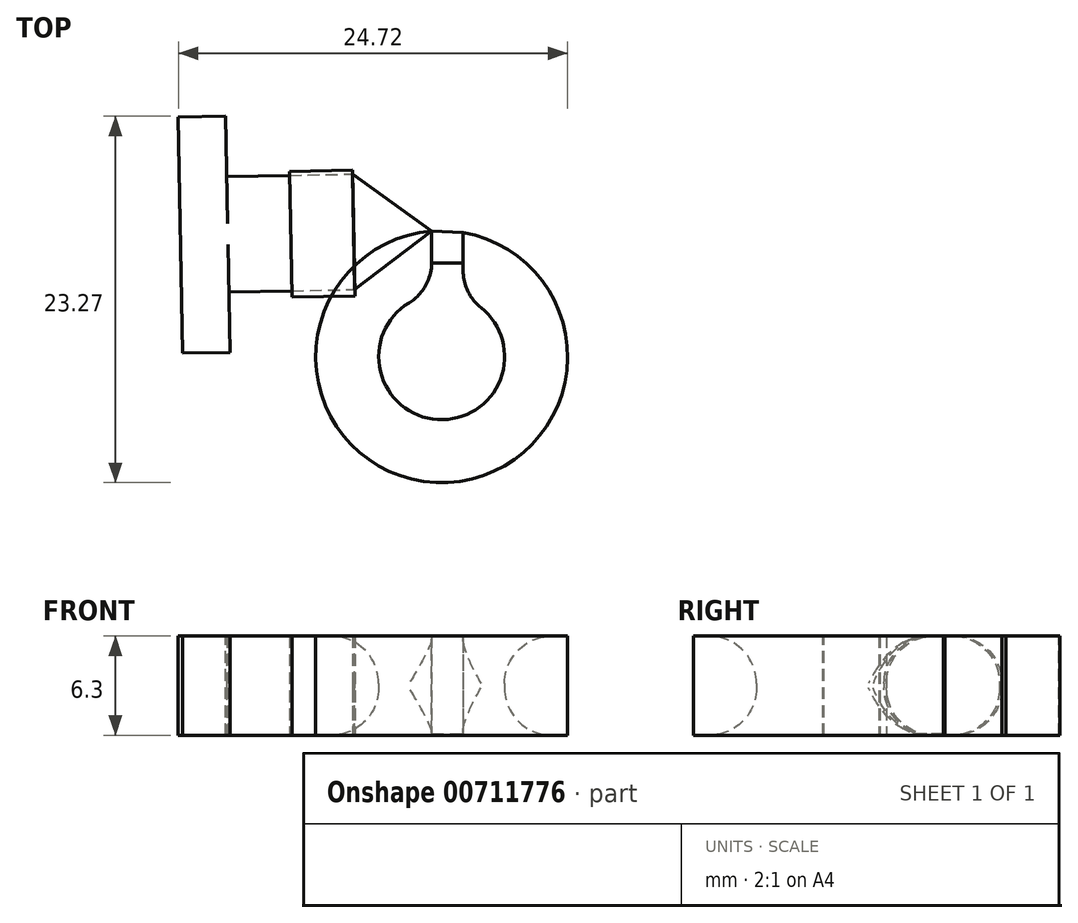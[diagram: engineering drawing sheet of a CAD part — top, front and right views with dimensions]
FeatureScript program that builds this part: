
annotation { "Feature Type Name" : "Feature", "Feature Type Description" : "" }
export const myFeature = defineFeature(function(context is Context, id is Id, definition is map)
    precondition{}
    {
        {
            var Q0;
            Q0=qCreatedBy(makeId("Top.planeOp"),FACE);
            var sketch = newSketch(context, id + "F0", { "sketchPlane" : qUnion([Q0])});
            skLineSegment(sketch, "E0.bottom", {"start": v(-5.02, 3.62) * mm, "end": v(0, 0) * mm});
            skLineSegment(sketch, "E0.top", {"start": v(-4.88, -3.71) * mm, "end": v(0, 0) * mm});
            skLineSegment(sketch, "E0.left", {"start": v(-5.02, 3.62) * mm, "end": v(-4.88, -3.71) * mm});
            skPoint(sketch, "E1", {"position": v(-4.95, -0.04) * mm});
            skSolve(sketch);
        }
        {
            var Q0;
            Q0 = qSketchRegion(id + "F0", true);
            extrude(context, id + "F1", {"entities" : qUnion([Q0]), "endBound" : BoundingType.SYMMETRIC, "depth" : 6.3 * mm, "offsetDistance" : 25 * mm});
        }
        {
            var Q0;
            Q0=makeQuery(id+"F1.opExtrude","SWEPT_FACE",FACE,{"disambiguationData":[OSD([sQuery(id+"F0.wireOp",EDGE,"E0.left")])]});
            var sketch = newSketch(context, id + "F2", { "sketchPlane" : qUnion([Q0])});
            skPoint(sketch, "E2", {"position": v(-0.05, -3.15) * mm});
            skPoint(sketch, "E3", {"position": v(-3.72, 0) * mm});
            skPoint(sketch, "E4", {"position": v(0, 0) * mm});
            skLineSegment(sketch, "E5.bottom", {"start": v(-0.72, -3.15) * mm, "end": v(0.62, -3.15) * mm});
            skLineSegment(sketch, "E5.top", {"start": v(-0.72, 3.15) * mm, "end": v(0.62, 3.15) * mm});
            skLineSegment(sketch, "E5.left", {"start": v(-3.72, -0.15) * mm, "end": v(-3.72, 0.15) * mm});
            skLineSegment(sketch, "E5.right", {"start": v(3.62, -0.15) * mm, "end": v(3.62, 0.15) * mm});
            skPoint(sketch, "E6", {"position": v(-3.69, 3.15) * mm});
            skPoint(sketch, "E7.visualSharp", {"position": v(-3.72, 3.15) * mm});
            skArc(sketch, "E7.filletArc", {"start": v(-0.72, 3.15) * mm, "mid": v(-2.84, 2.27) * mm, "end": v(-3.72, 0.15) * mm});
            skPoint(sketch, "E8.visualSharp", {"position": v(-3.72, -3.15) * mm});
            skArc(sketch, "E8.filletArc", {"start": v(-3.72, -0.15) * mm, "mid": v(-2.84, -2.27) * mm, "end": v(-0.72, -3.15) * mm});
            skPoint(sketch, "E9.visualSharp", {"position": v(3.62, -3.15) * mm});
            skArc(sketch, "E9.filletArc", {"start": v(0.62, -3.15) * mm, "mid": v(2.74, -2.27) * mm, "end": v(3.62, -0.15) * mm});
            skPoint(sketch, "E10.visualSharp", {"position": v(3.62, 3.15) * mm});
            skArc(sketch, "E10.filletArc", {"start": v(3.62, 0.15) * mm, "mid": v(2.74, 2.27) * mm, "end": v(0.62, 3.15) * mm});
            skSolve(sketch);
        }
        {
            var Q0;
            Q0=makeQuery(id+"F2.imprint","IMPRINT",FACE,{"disambiguationData":[TD([[makeQuery(id+"F2.imprint","IMPRINT",EDGE,{"derivedFrom":sQuery(id+"F2.wireOp",EDGE,"E5.bottom")}),1.0]])]});
            extrude(context, id + "F3", {"entities" : qUnion([Q0]), "depth" : 8 * mm, "offsetDistance" : 25 * mm});
        }
        {
            var Q0;
            Q0=makeQuery(id+"F3.opExtrude","CAP_FACE",FACE,{"disambiguationData":[OSD([sQuery(id+"F2.wireOp",EDGE,"E5.bottom"),sQuery(id+"F2.wireOp",EDGE,"E5.top"),sQuery(id+"F2.wireOp",EDGE,"E5.left"),sQuery(id+"F2.wireOp",EDGE,"E5.right")])],"isStart":false});
            cPlane(context, id + "F4", {"entities" : qUnion([Q0]), "cplaneType" : CPlaneType.OFFSET, "offset" : 0 * mm, "width" : 150 * mm, "height" : 150 * mm});
        }
        {
            var Q0;
            Q0=qCreatedBy(id+"F4.planeOp",FACE);
            var sketch = newSketch(context, id + "F5", { "sketchPlane" : qUnion([Q0])});
            skLineSegment(sketch, "E11.bottom", {"start": v(-7.55, -3.15) * mm, "end": v(7.45, -3.15) * mm});
            skLineSegment(sketch, "E11.top", {"start": v(-7.55, 3.15) * mm, "end": v(7.45, 3.15) * mm});
            skLineSegment(sketch, "E11.left", {"start": v(-7.55, -3.15) * mm, "end": v(-7.55, 3.15) * mm});
            skLineSegment(sketch, "E11.right", {"start": v(7.45, -3.15) * mm, "end": v(7.45, 3.15) * mm});
            skPoint(sketch, "E12", {"position": v(-3.72, 0) * mm});
            skPoint(sketch, "E13", {"position": v(-5.17, 0) * mm});
            skPoint(sketch, "E14", {"position": v(-0.05, 3.15) * mm});
            skSolve(sketch);
        }
        {
            var Q0;
            Q0=makeQuery(id+"F5.imprint","IMPRINT",FACE,{"disambiguationData":[TD([[makeQuery(id+"F5.imprint","IMPRINT",EDGE,{"derivedFrom":sQuery(id+"F5.wireOp",EDGE,"E11.bottom")}),1.0]])]});
            extrude(context, id + "F6", {"entities" : qUnion([Q0]), "operationType" : NewBodyOperationType.ADD, "depth" : 3 * mm, "offsetDistance" : 25 * mm});
        }
        {
            var Q0;
            Q0=qCreatedBy(makeId("Top.planeOp"),FACE);
            var sketch = newSketch(context, id + "F7", { "sketchPlane" : qUnion([Q0])});
            skArc(sketch, "E15", {"start": v(0, -4.03) * mm, "mid": v(0.26, -11.96) * mm, "end": v(2, -4.22) * mm});
            skArc(sketch, "E16", {"start": v(0, 0) * mm, "mid": v(0.27, -15.97) * mm, "end": v(2, -0.1) * mm});
            skLineSegment(sketch, "E17", {"start": v(2, -4.22) * mm, "end": v(2, -0.1) * mm});
            skLineSegment(sketch, "E18", {"start": v(0, -4.03) * mm, "end": v(0, 0) * mm});
            skLineSegment(sketch, "E19", {"start": v(2, -0.1) * mm, "end": v(0, 0) * mm, "construction": true});
            skSolve(sketch);
        }
        {
            var Q0;
            Q0 = qSketchRegion(id + "F7", true);
            extrude(context, id + "F8", {"entities" : qUnion([Q0]), "endBound" : BoundingType.SYMMETRIC, "depth" : 6.3 * mm, "offsetDistance" : 25 * mm});
        }
        {
            var Q0;
            Q0=makeQuery(id+"F8.opExtrude","SWEPT_FACE",FACE,{"disambiguationData":[OSD([sQuery(id+"F7.wireOp",EDGE,"E15")])]});
            fillet(context, id + "F9", {"entities" : qUnion([Q0]), "radius" : 3 * mm, "allowEdgeOverflow" : false});
        }
        {
            var Q0;
            Q0=qCreatedBy(id+"F4.planeOp",FACE);
            var sketch = newSketch(context, id + "F10", { "sketchPlane" : qUnion([Q0])});
            skLineSegment(sketch, "E20.bottom", {"start": v(-4.05, 3.15) * mm, "end": v(3.95, 3.15) * mm});
            skLineSegment(sketch, "E20.top", {"start": v(-4.05, -3.15) * mm, "end": v(3.95, -3.15) * mm});
            skLineSegment(sketch, "E20.left", {"start": v(-4.05, 3.15) * mm, "end": v(-4.05, -3.15) * mm});
            skLineSegment(sketch, "E20.right", {"start": v(3.95, 3.15) * mm, "end": v(3.95, -3.15) * mm});
            skPoint(sketch, "E21", {"position": v(-0.05, 3.15) * mm});
            skSolve(sketch);
        }
        {
            var Q0;
            Q0 = qSketchRegion(id + "F10", true);
            extrude(context, id + "F11", {"entities" : qUnion([Q0]), "oppositeDirection" : true, "depth" : 4 * mm, "offsetDistance" : 25 * mm});
        }
        {
            var Q0;
            Q0=makeQuery(id+"F11.opExtrude","SWEPT_BODY",BODY,{"disambiguationData":[OSD([sQuery(id+"F10.wireOp",EDGE,"E20.bottom"),sQuery(id+"F10.wireOp",EDGE,"E20.top"),sQuery(id+"F10.wireOp",EDGE,"E20.left"),sQuery(id+"F10.wireOp",EDGE,"E20.right")])]});
            transform(context, id + "F12", {"entities" : qUnion([Q0]), "transformType" : TransformType.TRANSLATION_3D, "dx" : 4 * mm, "dy" : 0 * mm, "dz" : 0 * mm, "makeCopy" : false});
        }
        {
            var Q0;
            Q0=qCreatedBy(makeId("Top.planeOp"),FACE);
            var sketch = newSketch(context, id + "F13", { "sketchPlane" : qUnion([Q0])});
            skLineSegment(sketch, "E22.bottom", {"start": v(0, 0) * mm, "end": v(2, -0.1) * mm});
            skLineSegment(sketch, "E22.top", {"start": v(0, -2.04) * mm, "end": v(2, -2.04) * mm});
            skLineSegment(sketch, "E22.left", {"start": v(0, 0) * mm, "end": v(0, -2.04) * mm});
            skLineSegment(sketch, "E22.right", {"start": v(2, -0.1) * mm, "end": v(2, -2.04) * mm});
            skSolve(sketch);
        }
        {
            var Q0;
            Q0 = qSketchRegion(id + "F13", true);
            extrude(context, id + "F14", {"entities" : qUnion([Q0]), "oppositeDirection" : true, "depth" : 0.1 * mm, "offsetDistance" : 25 * mm});
        }
        {
            var Q0;
            Q0=makeQuery(id+"F14.opExtrude","SWEPT_BODY",BODY,{"disambiguationData":[OSD([sQuery(id+"F13.wireOp",EDGE,"E22.bottom"),sQuery(id+"F13.wireOp",EDGE,"E22.top"),sQuery(id+"F13.wireOp",EDGE,"E22.left"),sQuery(id+"F13.wireOp",EDGE,"E22.right")])]});
            transform(context, id + "F15", {"entities" : qUnion([Q0]), "transformType" : TransformType.TRANSLATION_3D, "dx" : 0 * mm, "dy" : 0 * mm, "dz" : -3.05 * mm, "makeCopy" : false});
        }
    });
